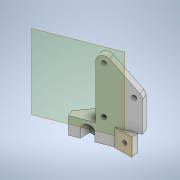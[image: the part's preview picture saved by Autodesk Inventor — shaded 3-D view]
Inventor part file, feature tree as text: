
AUTODESK INVENTOR PART (.ipt)
format: ipt  version: 2020 (Build 240168000, 168)  size: 305,152 bytes
history: native  units: mm
features: extrude x11, sketch x11, reference x9, other x8, projected_geometry x7, plane x3, thicken_offset x1
ambient origin geometry x8: Origin, YZ Plane, XZ Plane, XY Plane, X Axis, Y Axis, Z Axis, Center Point
bodies: Solid1 (feature_tree)
feature tree (50):
  plane  "Work Plane1"
  extrude  "Extrusion1"  Depth=6.0mm
  sketch  "Sketch4"  dims[d6=6.0mm d7=3.0mm]
  plane  "Work Plane2"
  extrude  "Extrusion2"  Depth=3.0mm
  extrude  "Extrusion3"  Depth=3.0mm
  extrude  "Extrusion4"  Depth=3.0mm TaperAngle=0.0deg
  extrude  "Extrusion5"  Depth=10.0mm
  plane  "Work Plane3"
  extrude  "Extrusion6"  Depth=10.0mm TaperAngle=0.0deg
  extrude  "Extrusion7"  Depth=7.0mm
  thicken_offset  "Thicken1"
  extrude  "Extrusion11"  Depth=10.0mm TaperAngle=0.0deg
  extrude  "Extrusion12"  Depth=2.0mm
  extrude  "Extrusion13"  Depth=10.0mm TaperAngle=0.0deg
  extrude  "Extrusion14"  Depth=10.0mm
  sketch  "Sketch2"  dims[d4=6.0mm d5=6.0mm]
  reference  "Reference4"
  reference  "Reference5"
  reference  "Reference6"
  reference  "Reference9"
  projected_geometry  "Projected Loop2"
  sketch  "Sketch5"  dims[d8=3.0mm d9=0.0mm d11=3.0mm]
  projected_geometry  "Projected Loop3"
  sketch  "Sketch6"  dims[d12=3.0mm d13=0.0mm d14=3.0mm d15=0.0mm]
  projected_geometry  "Projected Loop4"
  sketch  "Sketch7"  dims[d19=10.0mm d20=0.0mm d21=2.0mm]
  reference  "Reference10"
  reference  "Reference11"
  sketch  "Sketch8"  dims[d22=2.0mm d23=10.0mm d24=0.0mm]
  sketch  "Sketch9"  dims[d25=0.0mm d26=7.0mm]
  reference  "Reference12"
  reference  "Reference13"
  reference  "Reference14"
  sketch  "Sketch13"  dims[d27=5.0mm d28=10.0mm d29=0.0mm]
  projected_geometry  "Projected Loop7"
  sketch  "Sketch14"  dims[d30=2.0mm d31=2.0mm]
  projected_geometry  "Projected Loop8"
  sketch  "Sketch15"  dims[d32=2.0mm d33=10.0mm d34=0.0mm]
  projected_geometry  "Projected Loop9"
  sketch  "Sketch16"  dims[d35=0.2mm d36=0.2mm d57=10.0mm d58=10.0mm d59=10.0mm d60=6.0mm d61=6.0mm d62=6.0mm d63=4.0mm d64=0.0mm d65=2.0mm d66=10.0mm d67=2.0mm d68=10.0mm d69=2.0mm d70=4.0mm d71=0.0mm d72=4.0mm d73=0.0mm d74=6.0mm d75=4.0mm d76=0.0mm d54=0.5mm d55=0.872665mm d56=0.5mm]
  projected_geometry  "Projected Loop10"
  parser-record x1  (decoder bookkeeping rows leaked as tree rows — omitted from the tree; the rows remain in map.json)
  other  "leg_1.iam"
  other  "wh_ass_3:3"
  other  "screw_holder_2_3:2"
  other  "screw_holder_2_3:5"
  other  "screw_holder_2_3:1"
  other  "leg_holder_2:1"
  other  "tendon_wh_3:1"
note: 1 file-system path scrubbed to <path> (originals preserved in map.json)
